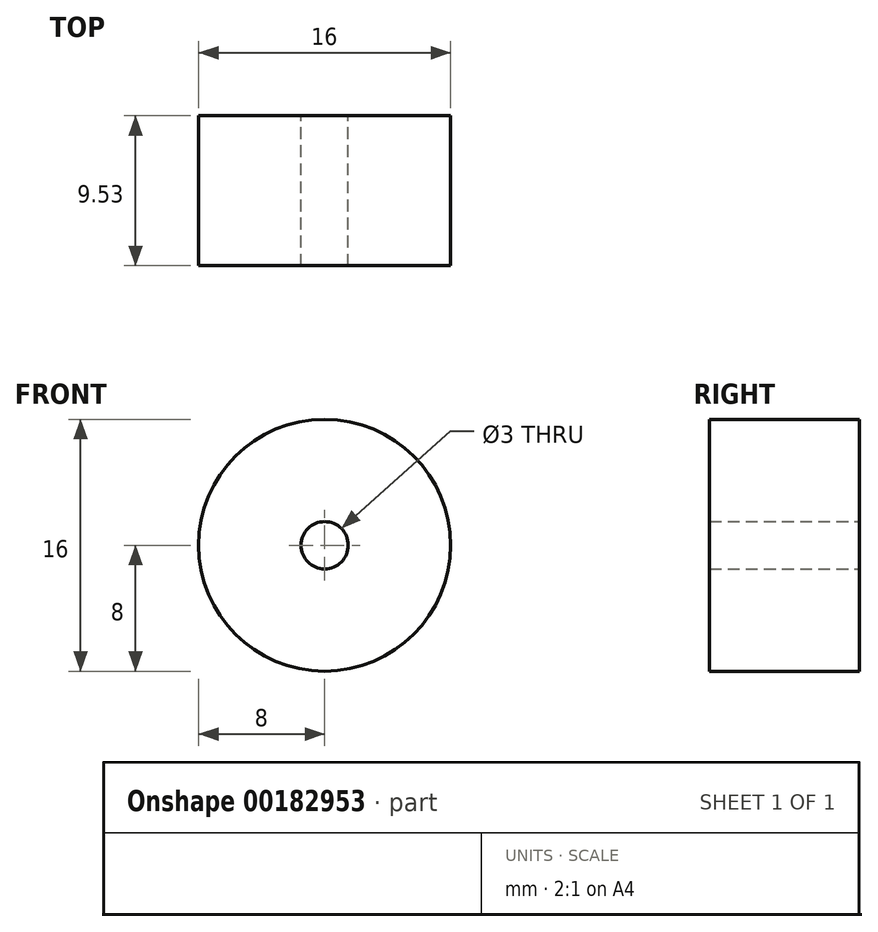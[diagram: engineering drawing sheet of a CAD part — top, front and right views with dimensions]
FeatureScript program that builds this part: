
annotation { "Feature Type Name" : "Feature", "Feature Type Description" : "" }
export const myFeature = defineFeature(function(context is Context, id is Id, definition is map)
    precondition{}
    {
        {
            var Q0;
            Q0=qCreatedBy(makeId("Front.planeOp"),FACE);
            var sketch = newSketch(context, id + "F0", { "sketchPlane" : qUnion([Q0])});
            skCircle(sketch, "E0", {"center": v(0, 0) * mm, "radius": 8 * mm});
            skCircle(sketch, "E1", {"center": v(0, 0) * mm, "radius": 1.5 * mm});
            skSolve(sketch);
        }
        {
            var Q0;
            Q0=makeQuery(id+"F0.imprint","IMPRINT",FACE,{"disambiguationData":[TD([[makeQuery(id+"F0.imprint","IMPRINT",EDGE,{"derivedFrom":sQuery(id+"F0.wireOp",EDGE,"E0")}),1.0]])]});
            var Q1;
            Q1=sQuery(id+"F0.wireOp",EDGE,"E1");
            var Q2;
            Q2=sQuery(id+"F0.wireOp",EDGE,"E0");
            extrude(context, id + "F1", {"entities" : qUnion([Q0]), "surfaceEntities" : qUnion([Q1, Q2]), "depth" : 9.52 * mm});
        }
    });
